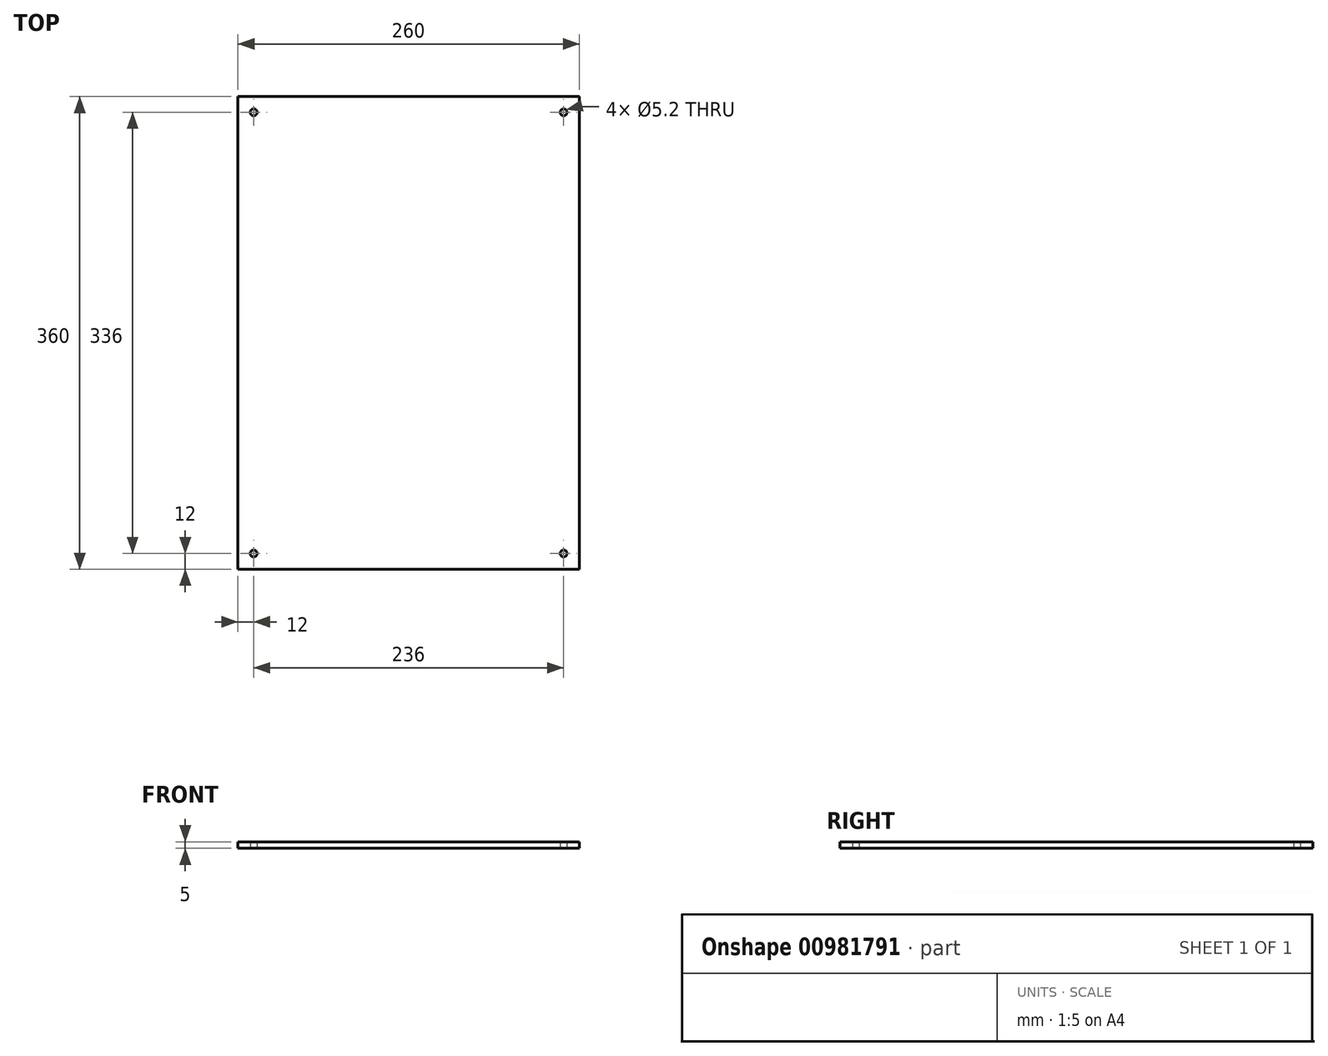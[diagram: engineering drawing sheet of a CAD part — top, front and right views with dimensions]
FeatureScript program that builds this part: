
annotation { "Feature Type Name" : "Feature", "Feature Type Description" : "" }
export const myFeature = defineFeature(function(context is Context, id is Id, definition is map)
    precondition{}
    {
        {
            var Q0;
            Q0=qCreatedBy(makeId("Top.planeOp"),FACE);
            var sketch = newSketch(context, id + "F0", { "sketchPlane" : qUnion([Q0])});
            skLineSegment(sketch, "E0.bottom", {"start": v(-130, 180) * mm, "end": v(130, 180) * mm});
            skLineSegment(sketch, "E0.top", {"start": v(-130, -180) * mm, "end": v(130, -180) * mm});
            skLineSegment(sketch, "E0.left", {"start": v(-130, 180) * mm, "end": v(-130, -180) * mm});
            skLineSegment(sketch, "E0.right", {"start": v(130, 180) * mm, "end": v(130, -180) * mm});
            skPoint(sketch, "E0.middle", {"position": v(0, 0) * mm});
            skCircle(sketch, "E1", {"center": v(-118, 168) * mm, "radius": 2.6 * mm});
            skCircle(sketch, "E2", {"center": v(118, 168) * mm, "radius": 2.6 * mm});
            skCircle(sketch, "E3.MirrorC", {"center": v(-118, -168) * mm, "radius": 2.6 * mm});
            skCircle(sketch, "E4.MirrorC", {"center": v(118, -168) * mm, "radius": 2.6 * mm});
            skSolve(sketch);
        }
        {
            assignVariable(context, id + "F1", {"name" : "CTP", "anyValue" : 5});
        }
        {
            var Q0;
            Q0=makeQuery(id+"F0.imprint","IMPRINT",FACE,{"disambiguationData":[TD([[makeQuery(id+"F0.imprint","IMPRINT",EDGE,{"derivedFrom":sQuery(id+"F0.wireOp",EDGE,"E0.bottom")}),-1.0]])]});
            extrude(context, id + "F2", {"entities" : qUnion([Q0]), "depth" : (getVariable(context, 'CTP')) * mm, "offsetDistance" : 25 * mm});
        }
    });
